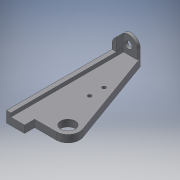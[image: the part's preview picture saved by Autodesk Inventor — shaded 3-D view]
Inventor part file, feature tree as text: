
AUTODESK INVENTOR PART (.ipt)
format: ipt  version: 2017 (Build 210142000, 142)  size: 185,344 bytes
history: native  units: mm
features: extrude x8, sketch x8, other x3, reference x1
ambient origin geometry x8: Origin, YZ Plane, XZ Plane, XY Plane, X Axis, Y Axis, Z Axis, Center Point
bodies: Solid1 (feature_tree)
feature tree (20):
  extrude  "Extrusion1"  Depth=5.0mm
  extrude  "Extrusion2"  Depth=30.0mm
  extrude  "Extrusion3"  Depth=10.0mm TaperAngle=0.0deg
  extrude  "Extrusion4"  Depth=10.0mm
  extrude  "Extrusion5"  Depth=4.0mm
  extrude  "Extrusion6"  Depth=5.1mm TaperAngle=0.0deg
  extrude  "Extrusion7"  Depth=6.0mm
  extrude  "Extrusion8"  Depth=5.0mm
  sketch  "Sketch1"  dims[d0=22.0mm d1=5.0mm]
  sketch  "Sketch2"  dims[d2=30.0mm d3=260.0mm]
  sketch  "Sketch3"  dims[d4=25.0mm d5=10.0mm d6=0.0mm]
  sketch  "Sketch4"  dims[d7=10.0mm d8=12.0mm]
  sketch  "Sketch5"  dims[d9=4.0mm d10=0.0mm d11=100.0mm]
  reference  "Reference2"
  sketch  "Sketch6"  dims[d12=10.0mm d13=0.0mm d14=5.1mm d15=0.0mm]
  sketch  "Sketch7"  dims[d16=10.0mm d17=0.0mm d18=6.0mm]
  sketch  "Sketch8"  dims[d19=10.0mm d20=0.0mm d21=5.0mm d22=20.0mm d23=35.0mm d24=80.0mm d25=10.0mm d26=0.0mm d27=1.0mm d28=1.0mm d29=0.0mm]
  other  "Assembly2.iam"
  other  "CJ2B16-100Z:1"
  other  "CJ2B16-100Z_5:1"
